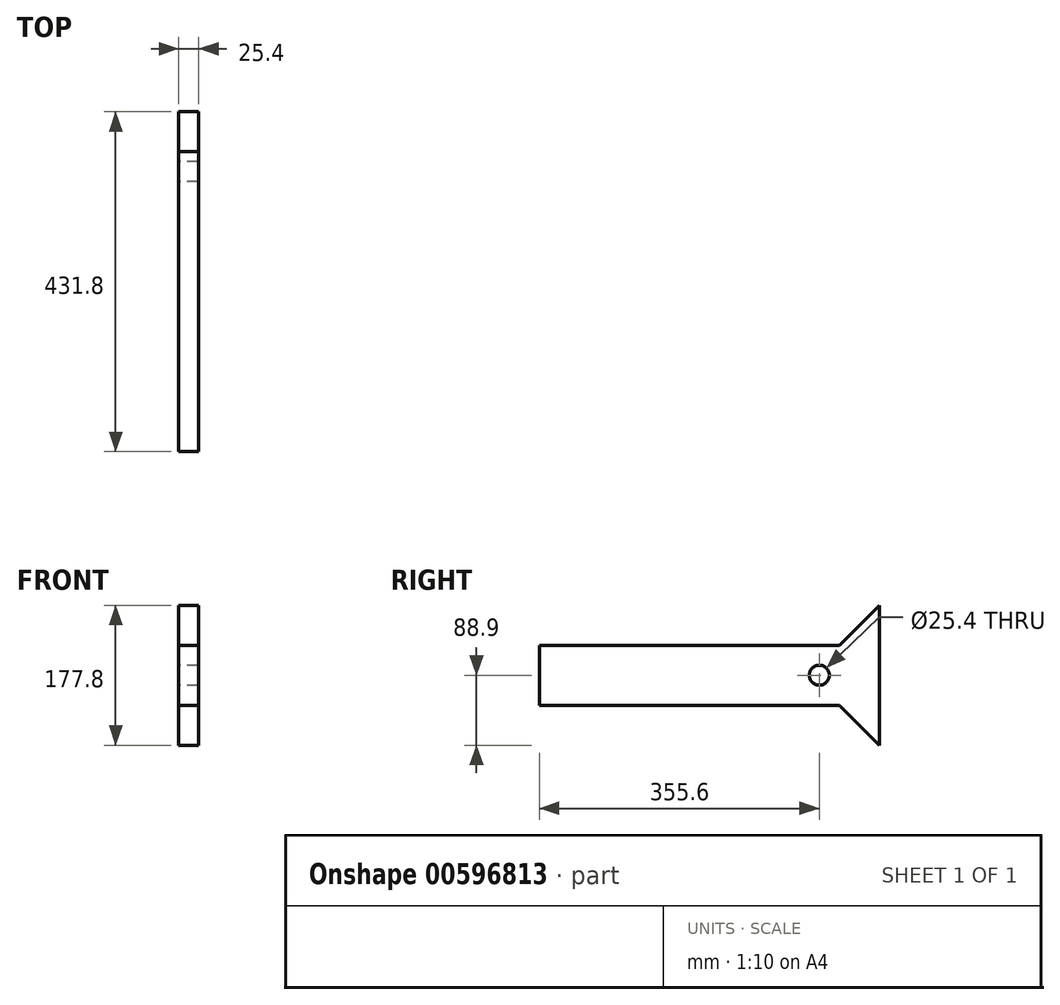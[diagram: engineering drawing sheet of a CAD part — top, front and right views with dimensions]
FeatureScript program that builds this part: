
annotation { "Feature Type Name" : "Feature", "Feature Type Description" : "" }
export const myFeature = defineFeature(function(context is Context, id is Id, definition is map)
    precondition{}
    {
        {
            var Q0;
            Q0=qCreatedBy(makeId("Right.planeOp"),FACE);
            var sketch = newSketch(context, id + "F0", { "sketchPlane" : qUnion([Q0])});
            skLineSegment(sketch, "E0.bottom", {"start": v(0, 0) * mm, "end": v(-381, 0) * mm});
            skLineSegment(sketch, "E0.top", {"start": v(0, -76.2) * mm, "end": v(-381, -76.2) * mm});
            skLineSegment(sketch, "E0.left", {"start": v(0, 0) * mm, "end": v(0, -76.2) * mm});
            skLineSegment(sketch, "E0.right", {"start": v(-381, 0) * mm, "end": v(-381, -76.2) * mm});
            skLineSegment(sketch, "E1.bottom", {"start": v(50.8, 50.8) * mm, "end": v(0, 50.8) * mm});
            skLineSegment(sketch, "E1.top", {"start": v(50.8, -127) * mm, "end": v(0, -127) * mm});
            skLineSegment(sketch, "E1.left", {"start": v(50.8, 50.8) * mm, "end": v(50.8, -127) * mm});
            skLineSegment(sketch, "E1.right", {"start": v(0, 50.8) * mm, "end": v(0, -127) * mm});
            skLineSegment(sketch, "E2", {"start": v(0, 0) * mm, "end": v(50.8, 50.8) * mm});
            skLineSegment(sketch, "E3", {"start": v(0, -76.2) * mm, "end": v(50.8, -127) * mm});
            skCircle(sketch, "E4", {"center": v(-25.4, -38.1) * mm, "radius": 12.7 * mm});
            skPoint(sketch, "E4.centerSnap0", {"position": v(0, -38.1) * mm});
            skSolve(sketch);
        }
        {
            var Q0;
            {var subQ1=sQuery(id+"F0.wireOp",EDGE,"E0.bottom");Q0=makeQuery(id+"F0.imprint","IMPRINT",FACE,{"disambiguationData":[TD([[makeQuery(id+"F0.imprint","IMPRINT",EDGE,{"derivedFrom":subQ1}),1.0]])]});}
            var Q1;
            Q1=makeQuery(id+"F0.imprint","IMPRINT",FACE,{"disambiguationData":[TD([[makeQuery(id+"F0.imprint","IMPRINT",EDGE,{"derivedFrom":sQuery(id+"F0.wireOp",EDGE,"E1.left")}),-1.0]])]});
            extrude(context, id + "F1", {"entities" : qUnion([Q0, Q1]), "depth" : 25.4 * mm, "offsetDistance" : 25.4 * mm});
        }
    });
